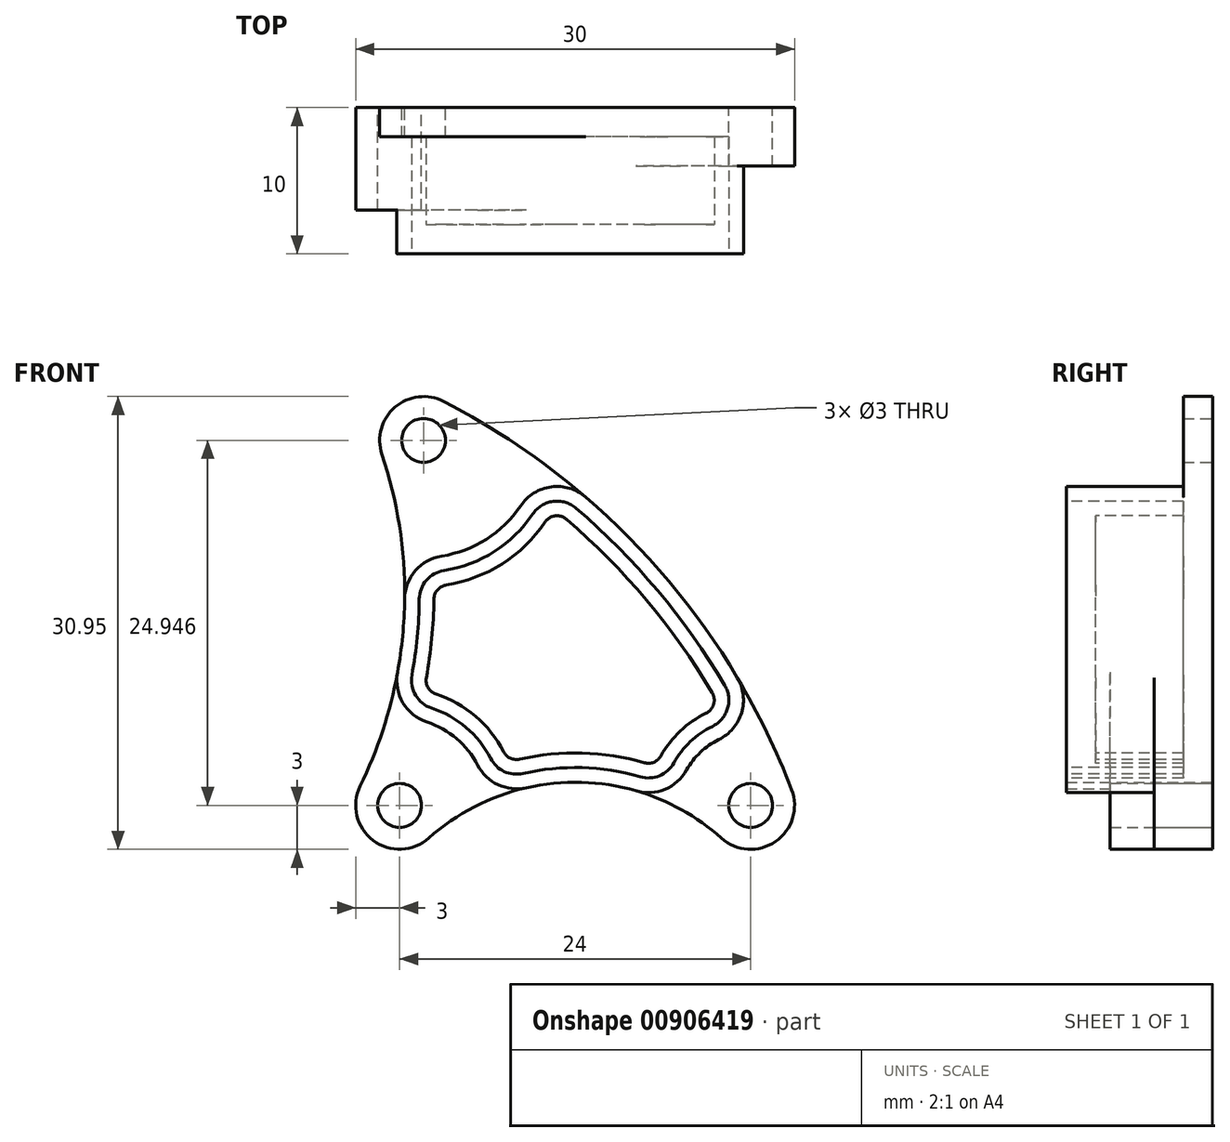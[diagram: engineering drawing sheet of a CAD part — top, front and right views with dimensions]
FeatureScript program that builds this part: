
annotation { "Feature Type Name" : "Feature", "Feature Type Description" : "" }
export const myFeature = defineFeature(function(context is Context, id is Id, definition is map)
    precondition{}
    {
        {
            var Q0;
            Q0=qCreatedBy(makeId("Front.planeOp"),FACE);
            var sketch = newSketch(context, id + "F0", { "sketchPlane" : qUnion([Q0])});
            skArc(sketch, "E0", {"start": v(-2, -2.24) * mm, "mid": v(1.7, -2.47) * mm, "end": v(2.8, 1.07) * mm});
            skArc(sketch, "E1", {"start": v(-26.7, 1.32) * mm, "mid": v(-25.8, -2.4) * mm, "end": v(-22, -2.24) * mm});
            skArc(sketch, "E2", {"start": v(-20.99, 27.61) * mm, "mid": v(-24.31, 27.22) * mm, "end": v(-25.2, 24) * mm});
            skArc(sketch, "E3", {"start": v(2.8, 1.07) * mm, "mid": v(-6.65, 16.54) * mm, "end": v(-20.99, 27.61) * mm});
            skArc(sketch, "E4", {"start": v(-26.7, 1.32) * mm, "mid": v(-23.72, 12.5) * mm, "end": v(-25.2, 24) * mm});
            skArc(sketch, "E5", {"start": v(-2, -2.24) * mm, "mid": v(-12, 1.58) * mm, "end": v(-22, -2.24) * mm});
            skSolve(sketch);
        }
        {
            var Q0;
            Q0=makeQuery(id+"F0.imprint","IMPRINT",FACE,{"disambiguationData":[TD([[makeQuery(id+"F0.imprint","IMPRINT",EDGE,{"derivedFrom":sQuery(id+"F0.wireOp",EDGE,"E0")}),1.0]])]});
            extrude(context, id + "F1", {"entities" : qUnion([Q0]), "depth" : 2 * mm, "offsetDistance" : 25 * mm});
        }
        {
            var Q0;
            Q0=makeQuery(id+"F1.opExtrude","CAP_FACE",FACE,{"disambiguationData":[OSD([sQuery(id+"F0.wireOp",EDGE,"E0"),sQuery(id+"F0.wireOp",EDGE,"E1"),sQuery(id+"F0.wireOp",EDGE,"E2"),sQuery(id+"F0.wireOp",EDGE,"E3"),sQuery(id+"F0.wireOp",EDGE,"E4"),sQuery(id+"F0.wireOp",EDGE,"E5")])],"isStart":false});
            var sketch = newSketch(context, id + "F2", { "sketchPlane" : qUnion([Q0])});
            skArc(sketch, "E6", {"start": v(-21.12, 17.04) * mm, "mid": v(-18.06, 18.2) * mm, "end": v(-15.72, 20.48) * mm});
            skArc(sketch, "E7", {"start": v(-2.18, 4.5) * mm, "mid": v(-3.44, 3.63) * mm, "end": v(-4.37, 2.42) * mm});
            skArc(sketch, "E8", {"start": v(-18.67, 2.75) * mm, "mid": v(-20.1, 4.57) * mm, "end": v(-22.13, 5.7) * mm});
            skArc(sketch, "E9.0", {"start": v(-0.91, 8.73) * mm, "mid": v(-5.6, 15.32) * mm, "end": v(-11.28, 21.07) * mm});
            skArc(sketch, "E10.0", {"start": v(-24.14, 9.09) * mm, "mid": v(-23.8, 11.6) * mm, "end": v(-23.66, 14.11) * mm});
            skArc(sketch, "E11.0", {"start": v(-7.83, 1) * mm, "mid": v(-11.57, 1.58) * mm, "end": v(-15.34, 1.2) * mm});
            skPoint(sketch, "E12.newPointB", {"position": v(-20.99, 27.61) * mm});
            skArc(sketch, "E12.filletArc", {"start": v(-11.28, 21.07) * mm, "mid": v(-13.64, 21.77) * mm, "end": v(-15.72, 20.48) * mm});
            skPoint(sketch, "E13.newPointA", {"position": v(2.8, 1.07) * mm});
            skArc(sketch, "E13.filletArc", {"start": v(-2.18, 4.5) * mm, "mid": v(-0.62, 6.34) * mm, "end": v(-0.91, 8.73) * mm});
            skPoint(sketch, "E14.newPointB", {"position": v(-2, -2.24) * mm});
            skArc(sketch, "E14.filletArc", {"start": v(-7.83, 1) * mm, "mid": v(-5.85, 1.1) * mm, "end": v(-4.37, 2.42) * mm});
            skPoint(sketch, "E15.newPointA", {"position": v(-22, -2.24) * mm});
            skArc(sketch, "E15.filletArc", {"start": v(-18.67, 2.75) * mm, "mid": v(-17.27, 1.41) * mm, "end": v(-15.34, 1.2) * mm});
            skPoint(sketch, "E16.newPointA", {"position": v(-26.7, 1.32) * mm});
            skArc(sketch, "E16.filletArc", {"start": v(-24.14, 9.09) * mm, "mid": v(-23.77, 7.02) * mm, "end": v(-22.13, 5.7) * mm});
            skPoint(sketch, "E17.newPointA", {"position": v(-25.2, 24) * mm});
            skArc(sketch, "E17.filletArc", {"start": v(-21.12, 17.04) * mm, "mid": v(-22.92, 16.04) * mm, "end": v(-23.66, 14.11) * mm});
            skSolve(sketch);
        }
        {
            var Q0;
            Q0=makeQuery(id+"F2.imprint","IMPRINT",FACE,{"disambiguationData":[TD([[makeQuery(id+"F2.imprint","IMPRINT",EDGE,{"derivedFrom":sQuery(id+"F2.wireOp",EDGE,"E6")}),-1.0]])]});
            extrude(context, id + "F3", {"entities" : qUnion([Q0]), "operationType" : NewBodyOperationType.ADD, "depth" : 8 * mm, "offsetDistance" : 25 * mm});
        }
        {
            var Q0;
            {var subQ0=sQuery(id+"F0.wireOp",EDGE,"E5");var subQ1=sQuery(id+"F0.wireOp",EDGE,"E4");var subQ2=sQuery(id+"F0.wireOp",EDGE,"E1");Q0=makeQuery(id+"F3.boolean.opBoolean","SPLIT",FACE,{"disambiguationData":[TD([makeQuery(id+"F1.opExtrude","SWEPT_FACE",FACE,{"disambiguationData":[OSD([subQ2])]})])],"derivedFrom":makeQuery(id+"F1.opExtrude","CAP_FACE",FACE,{"disambiguationData":[OSD([sQuery(id+"F0.wireOp",EDGE,"E0"),subQ2,sQuery(id+"F0.wireOp",EDGE,"E2"),sQuery(id+"F0.wireOp",EDGE,"E3"),subQ1,subQ0])],"isStart":false})});}
            var sketch = newSketch(context, id + "F4", { "sketchPlane" : qUnion([Q0])});
            skArc(sketch, "E18.0.0", {"start": v(-15.34, 1.2) * mm, "mid": v(-17.27, 1.41) * mm, "end": v(-18.67, 2.75) * mm});
            skArc(sketch, "E18.0.1", {"start": v(-18.67, 2.75) * mm, "mid": v(-20.1, 4.57) * mm, "end": v(-22.13, 5.7) * mm});
            skArc(sketch, "E18.0.2", {"start": v(-22.13, 5.7) * mm, "mid": v(-23.77, 7.02) * mm, "end": v(-24.14, 9.09) * mm});
            skArc(sketch, "E18.0.3", {"start": v(-24.14, 9.09) * mm, "mid": v(-25.15, 5.12) * mm, "end": v(-26.7, 1.32) * mm});
            skArc(sketch, "E18.0.4", {"start": v(-26.7, 1.32) * mm, "mid": v(-25.8, -2.4) * mm, "end": v(-22, -2.24) * mm});
            skArc(sketch, "E18.0.5", {"start": v(-22, -2.24) * mm, "mid": v(-18.89, -0.1) * mm, "end": v(-15.34, 1.2) * mm});
            skSolve(sketch);
        }
        {
            var Q0;
            Q0=qSketchRegion(id+"F4",true);
            extrude(context, id + "F5", {"entities" : qUnion([Q0]), "operationType" : NewBodyOperationType.ADD, "depth" : 5 * mm, "offsetDistance" : 25 * mm});
        }
        {
            var Q0;
            {var subQ0=sQuery(id+"F0.wireOp",EDGE,"E5");var subQ1=sQuery(id+"F0.wireOp",EDGE,"E3");var subQ2=sQuery(id+"F0.wireOp",EDGE,"E0");Q0=makeQuery(id+"F3.boolean.opBoolean","SPLIT",FACE,{"disambiguationData":[TD([makeQuery(id+"F1.opExtrude","SWEPT_FACE",FACE,{"disambiguationData":[OSD([subQ2])]})])],"derivedFrom":makeQuery(id+"F1.opExtrude","CAP_FACE",FACE,{"disambiguationData":[OSD([subQ2,sQuery(id+"F0.wireOp",EDGE,"E1"),sQuery(id+"F0.wireOp",EDGE,"E2"),subQ1,sQuery(id+"F0.wireOp",EDGE,"E4"),subQ0])],"isStart":false})});}
            var sketch = newSketch(context, id + "F6", { "sketchPlane" : qUnion([Q0])});
            skArc(sketch, "E19.0.0", {"start": v(-0.91, 8.73) * mm, "mid": v(-0.62, 6.34) * mm, "end": v(-2.18, 4.5) * mm});
            skArc(sketch, "E19.0.1", {"start": v(-2.18, 4.5) * mm, "mid": v(-3.44, 3.63) * mm, "end": v(-4.37, 2.42) * mm});
            skArc(sketch, "E19.0.2", {"start": v(-4.37, 2.42) * mm, "mid": v(-5.85, 1.1) * mm, "end": v(-7.83, 1) * mm});
            skArc(sketch, "E19.0.3", {"start": v(-7.83, 1) * mm, "mid": v(-4.73, -0.3) * mm, "end": v(-2, -2.24) * mm});
            skArc(sketch, "E19.0.4", {"start": v(-2, -2.24) * mm, "mid": v(1.7, -2.47) * mm, "end": v(2.8, 1.07) * mm});
            skArc(sketch, "E19.0.5", {"start": v(2.8, 1.07) * mm, "mid": v(1.1, 4.98) * mm, "end": v(-0.91, 8.73) * mm});
            skSolve(sketch);
        }
        {
            var Q0;
            Q0=qSketchRegion(id+"F6",true);
            extrude(context, id + "F7", {"entities" : qUnion([Q0]), "operationType" : NewBodyOperationType.ADD, "depth" : 2 * mm, "offsetDistance" : 25 * mm});
        }
        {
            var Q0;
            Q0=makeQuery(id+"F3.opExtrude","CAP_FACE",FACE,{"disambiguationData":[OSD([sQuery(id+"F2.wireOp",EDGE,"E6"),sQuery(id+"F2.wireOp",EDGE,"E7"),sQuery(id+"F2.wireOp",EDGE,"E8"),sQuery(id+"F2.wireOp",EDGE,"E9.0"),sQuery(id+"F2.wireOp",EDGE,"E10.0"),sQuery(id+"F2.wireOp",EDGE,"E11.0"),sQuery(id+"F2.wireOp",EDGE,"E12.filletArc"),sQuery(id+"F2.wireOp",EDGE,"E13.filletArc"),sQuery(id+"F2.wireOp",EDGE,"E14.filletArc"),sQuery(id+"F2.wireOp",EDGE,"E15.filletArc"),sQuery(id+"F2.wireOp",EDGE,"E16.filletArc"),sQuery(id+"F2.wireOp",EDGE,"E17.filletArc")])],"isStart":false});
            var sketch = newSketch(context, id + "F8", { "sketchPlane" : qUnion([Q0])});
            skArc(sketch, "E20.0", {"start": v(-20.97, 16.05) * mm, "mid": v(-22.17, 15.39) * mm, "end": v(-22.66, 14.1) * mm});
            skArc(sketch, "E20.1", {"start": v(-15.56, 2.18) * mm, "mid": v(-11.54, 2.58) * mm, "end": v(-7.55, 1.95) * mm});
            skArc(sketch, "E20.2", {"start": v(-17.78, 3.21) * mm, "mid": v(-16.85, 2.32) * mm, "end": v(-15.56, 2.18) * mm});
            skArc(sketch, "E20.3", {"start": v(-21.82, 6.65) * mm, "mid": v(-19.46, 5.33) * mm, "end": v(-17.78, 3.21) * mm});
            skArc(sketch, "E20.4", {"start": v(-23.16, 8.9) * mm, "mid": v(-22.91, 7.53) * mm, "end": v(-21.82, 6.65) * mm});
            skArc(sketch, "E20.5", {"start": v(-7.55, 1.95) * mm, "mid": v(-6.24, 2.03) * mm, "end": v(-5.25, 2.9) * mm});
            skArc(sketch, "E20.6", {"start": v(-22.66, 14.1) * mm, "mid": v(-22.8, 11.5) * mm, "end": v(-23.16, 8.9) * mm});
            skArc(sketch, "E20.7", {"start": v(-5.25, 2.9) * mm, "mid": v(-4.13, 4.36) * mm, "end": v(-2.62, 5.4) * mm});
            skArc(sketch, "E20.8", {"start": v(-2.62, 5.4) * mm, "mid": v(-1.58, 6.62) * mm, "end": v(-1.77, 8.22) * mm});
            skArc(sketch, "E20.9", {"start": v(-1.77, 8.22) * mm, "mid": v(-6.36, 14.68) * mm, "end": v(-11.93, 20.32) * mm});
            skArc(sketch, "E20.10", {"start": v(-11.93, 20.32) * mm, "mid": v(-13.5, 20.78) * mm, "end": v(-14.9, 19.92) * mm});
            skArc(sketch, "E20.11", {"start": v(-14.9, 19.92) * mm, "mid": v(-17.53, 17.35) * mm, "end": v(-20.97, 16.05) * mm});
            skSolve(sketch);
        }
        {
            var Q0;
            Q0=makeQuery(id+"F8.imprint","IMPRINT",FACE,{"disambiguationData":[TD([[makeQuery(id+"F8.imprint","IMPRINT",EDGE,{"derivedFrom":sQuery(id+"F8.wireOp",EDGE,"E20.0")}),1.0]])]});
            extrude(context, id + "F9", {"entities" : qUnion([Q0]), "operationType" : NewBodyOperationType.REMOVE, "oppositeDirection" : true, "depth" : 2 * mm, "offsetDistance" : 25 * mm});
        }
        {
            var Q0;
            Q0=makeQuery(id+"F9.boolean.opBoolean","COPY",FACE,{"derivedFrom":makeQuery(id+"F9.opExtrude","CAP_FACE",FACE,{"disambiguationData":[OSD([sQuery(id+"F8.wireOp",EDGE,"E20.0"),sQuery(id+"F8.wireOp",EDGE,"E20.1"),sQuery(id+"F8.wireOp",EDGE,"E20.2"),sQuery(id+"F8.wireOp",EDGE,"E20.3"),sQuery(id+"F8.wireOp",EDGE,"E20.4"),sQuery(id+"F8.wireOp",EDGE,"E20.5"),sQuery(id+"F8.wireOp",EDGE,"E20.6"),sQuery(id+"F8.wireOp",EDGE,"E20.7"),sQuery(id+"F8.wireOp",EDGE,"E20.8"),sQuery(id+"F8.wireOp",EDGE,"E20.9"),sQuery(id+"F8.wireOp",EDGE,"E20.10"),sQuery(id+"F8.wireOp",EDGE,"E20.11")])],"isStart":false})});
            var sketch = newSketch(context, id + "F10", { "sketchPlane" : qUnion([Q0])});
            skArc(sketch, "E21.0", {"start": v(-15.78, 3.16) * mm, "mid": v(-11.51, 3.58) * mm, "end": v(-7.28, 2.91) * mm});
            skArc(sketch, "E21.1", {"start": v(-12.58, 19.56) * mm, "mid": v(-13.37, 19.8) * mm, "end": v(-14.07, 19.36) * mm});
            skArc(sketch, "E21.2", {"start": v(-2.63, 7.7) * mm, "mid": v(-7.13, 14.04) * mm, "end": v(-12.58, 19.56) * mm});
            skArc(sketch, "E21.3", {"start": v(-3.05, 6.3) * mm, "mid": v(-2.53, 6.91) * mm, "end": v(-2.63, 7.7) * mm});
            skArc(sketch, "E21.4", {"start": v(-6.12, 3.4) * mm, "mid": v(-4.81, 5.08) * mm, "end": v(-3.05, 6.3) * mm});
            skArc(sketch, "E21.5", {"start": v(-14.07, 19.36) * mm, "mid": v(-17, 16.5) * mm, "end": v(-20.81, 15.07) * mm});
            skArc(sketch, "E21.6", {"start": v(-7.28, 2.91) * mm, "mid": v(-6.62, 2.95) * mm, "end": v(-6.12, 3.4) * mm});
            skArc(sketch, "E21.7", {"start": v(-20.81, 15.07) * mm, "mid": v(-21.41, 14.73) * mm, "end": v(-21.66, 14.1) * mm});
            skArc(sketch, "E21.8", {"start": v(-21.66, 14.1) * mm, "mid": v(-21.8, 11.4) * mm, "end": v(-22.18, 8.73) * mm});
            skArc(sketch, "E21.9", {"start": v(-22.18, 8.73) * mm, "mid": v(-22.05, 8.04) * mm, "end": v(-21.5, 7.6) * mm});
            skArc(sketch, "E21.10", {"start": v(-21.5, 7.6) * mm, "mid": v(-18.81, 6.09) * mm, "end": v(-16.9, 3.67) * mm});
            skArc(sketch, "E21.11", {"start": v(-16.9, 3.67) * mm, "mid": v(-16.43, 3.23) * mm, "end": v(-15.78, 3.16) * mm});
            skSolve(sketch);
        }
        {
            var Q0;
            Q0=makeQuery(id+"F10.imprint","IMPRINT",FACE,{"disambiguationData":[TD([[makeQuery(id+"F10.imprint","IMPRINT",EDGE,{"derivedFrom":sQuery(id+"F10.wireOp",EDGE,"E21.0")}),1.0]])]});
            extrude(context, id + "F11", {"entities" : qUnion([Q0]), "operationType" : NewBodyOperationType.REMOVE, "oppositeDirection" : true, "depth" : 6 * mm, "offsetDistance" : 25 * mm});
        }
        {
            var Q0;
            Q0=qCreatedBy(makeId("Front.planeOp"),FACE);
            var sketch = newSketch(context, id + "F12", { "sketchPlane" : qUnion([Q0])});
            skCircle(sketch, "E22", {"center": v(-22.36, 24.95) * mm, "radius": 1.5 * mm});
            skCircle(sketch, "E23", {"center": v(0, 0) * mm, "radius": 1.5 * mm});
            skCircle(sketch, "E24", {"center": v(-24, 0) * mm, "radius": 1.5 * mm});
            skSolve(sketch);
        }
        {
            var Q0;
            Q0=qSketchRegion(id+"F12",true);
            extrude(context, id + "F13", {"entities" : qUnion([Q0]), "operationType" : NewBodyOperationType.REMOVE, "endBound" : BoundingType.THROUGH_ALL, "depth" : 25 * mm, "offsetDistance" : 25 * mm});
        }
    });
